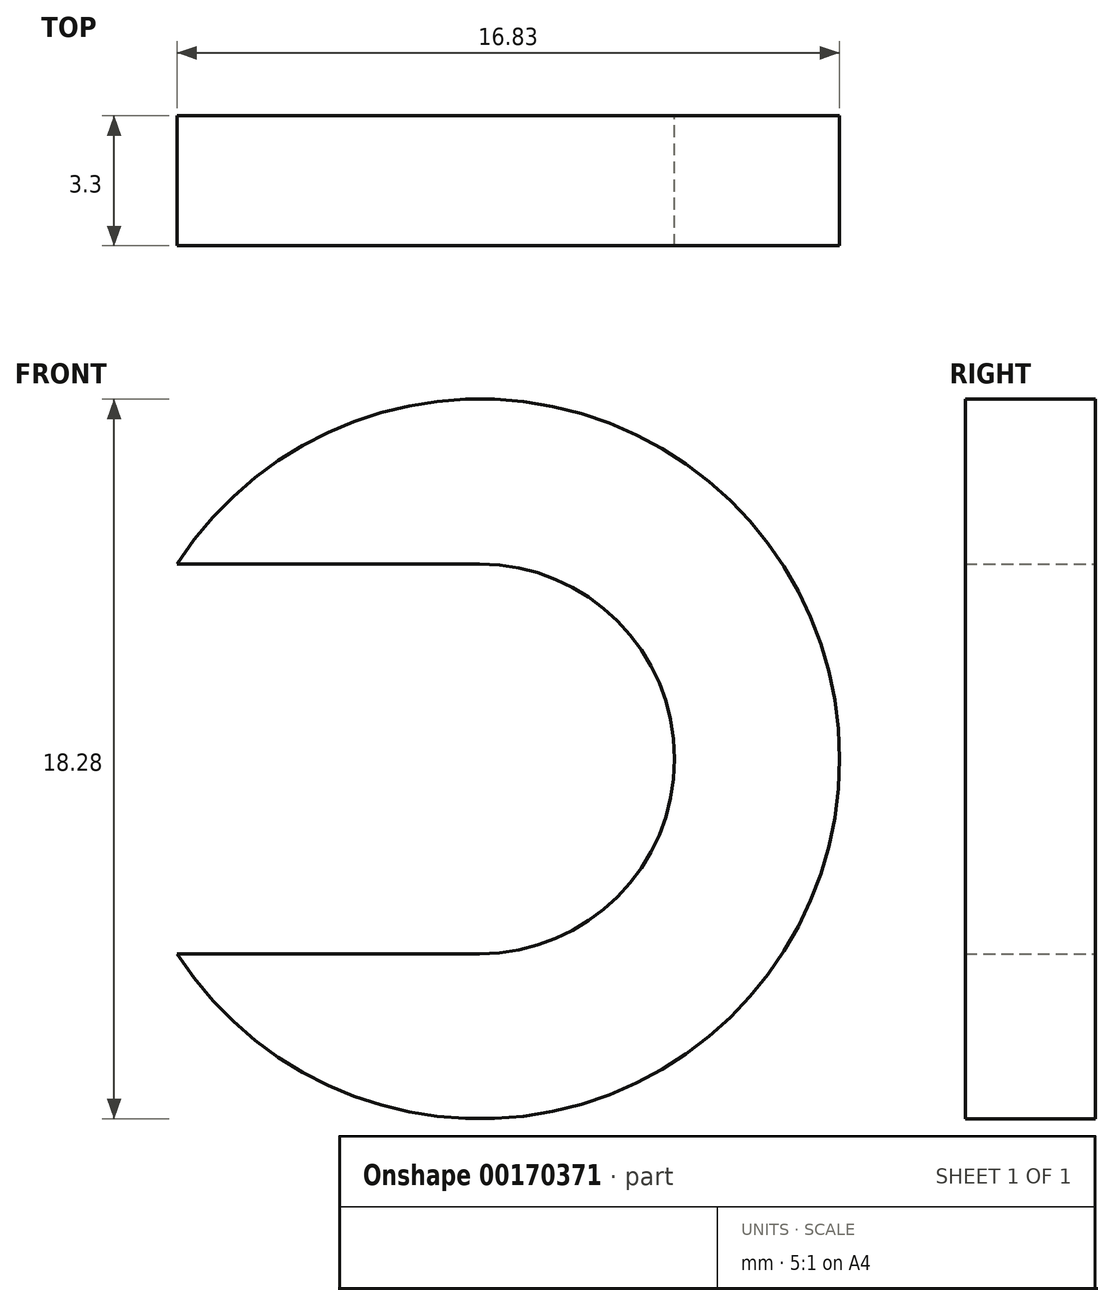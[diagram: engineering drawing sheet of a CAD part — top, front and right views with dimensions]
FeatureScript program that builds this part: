
annotation { "Feature Type Name" : "Feature", "Feature Type Description" : "" }
export const myFeature = defineFeature(function(context is Context, id is Id, definition is map)
    precondition{}
    {
        {
            var Q0;
            Q0=qCreatedBy(makeId("Front.planeOp"),FACE);
            var sketch = newSketch(context, id + "F0", { "sketchPlane" : qUnion([Q0])});
            skArc(sketch, "E0", {"start": v(-7.69, -4.95) * mm, "mid": v(9.14, 0) * mm, "end": v(-7.69, 4.95) * mm});
            skArc(sketch, "E1", {"start": v(0, -4.95) * mm, "mid": v(4.95, 0) * mm, "end": v(0, 4.95) * mm});
            skLineSegment(sketch, "E2", {"start": v(0, 4.95) * mm, "end": v(-7.69, 4.95) * mm});
            skLineSegment(sketch, "E3", {"start": v(0, -4.95) * mm, "end": v(-7.69, -4.95) * mm});
            skSolve(sketch);
        }
        {
            var Q0;
            Q0 = qSketchRegion(id + "F0", true);
            extrude(context, id + "F1", {"entities" : qUnion([Q0]), "depth" : 3.3 * mm});
        }
    });
